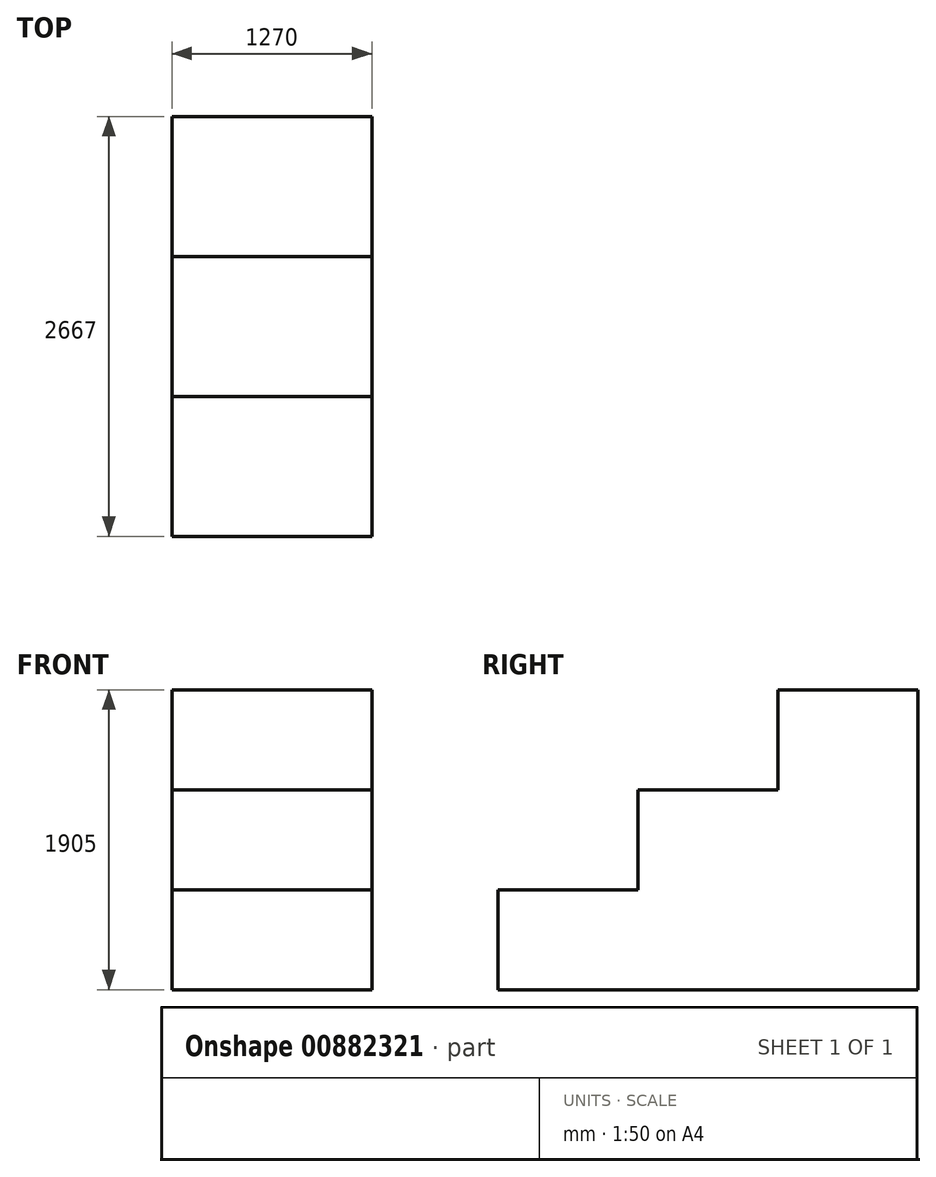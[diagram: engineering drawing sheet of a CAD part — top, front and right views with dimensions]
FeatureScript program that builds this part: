
annotation { "Feature Type Name" : "Feature", "Feature Type Description" : "" }
export const myFeature = defineFeature(function(context is Context, id is Id, definition is map)
    precondition{}
    {
        {
            var Q0;
            Q0=qCreatedBy(makeId("Right.planeOp"),FACE);
            var sketch = newSketch(context, id + "F0", { "sketchPlane" : qUnion([Q0])});
            skLineSegment(sketch, "E0", {"start": v(0, -635) * mm, "end": v(-1333.5, -635) * mm});
            skLineSegment(sketch, "E1", {"start": v(-1333.5, -635) * mm, "end": v(-1333.5, 0) * mm});
            skLineSegment(sketch, "E2", {"start": v(-1333.5, 0) * mm, "end": v(-444.5, 0) * mm});
            skLineSegment(sketch, "E3", {"start": v(-444.5, 0) * mm, "end": v(-444.5, 635) * mm});
            skLineSegment(sketch, "E4", {"start": v(-444.5, 635) * mm, "end": v(444.5, 635) * mm});
            skLineSegment(sketch, "E5", {"start": v(444.5, 635) * mm, "end": v(444.5, 1270) * mm});
            skLineSegment(sketch, "E6", {"start": v(444.5, 1270) * mm, "end": v(1333.5, 1270) * mm});
            skLineSegment(sketch, "E7", {"start": v(1333.5, 1270) * mm, "end": v(1333.5, -635) * mm});
            skLineSegment(sketch, "E8", {"start": v(1333.5, -635) * mm, "end": v(0, -635) * mm});
            skSolve(sketch);
        }
        {
            var Q0;
            Q0=makeQuery(id+"F0.imprint","IMPRINT",FACE,{"disambiguationData":[TD([[makeQuery(id+"F0.imprint","IMPRINT",EDGE,{"derivedFrom":sQuery(id+"F0.wireOp",EDGE,"E0")}),-1.0]])]});
            extrude(context, id + "F1", {"entities" : qUnion([Q0]), "depth" : 1270 * mm, "offsetDistance" : 25.4 * mm});
        }
    });
